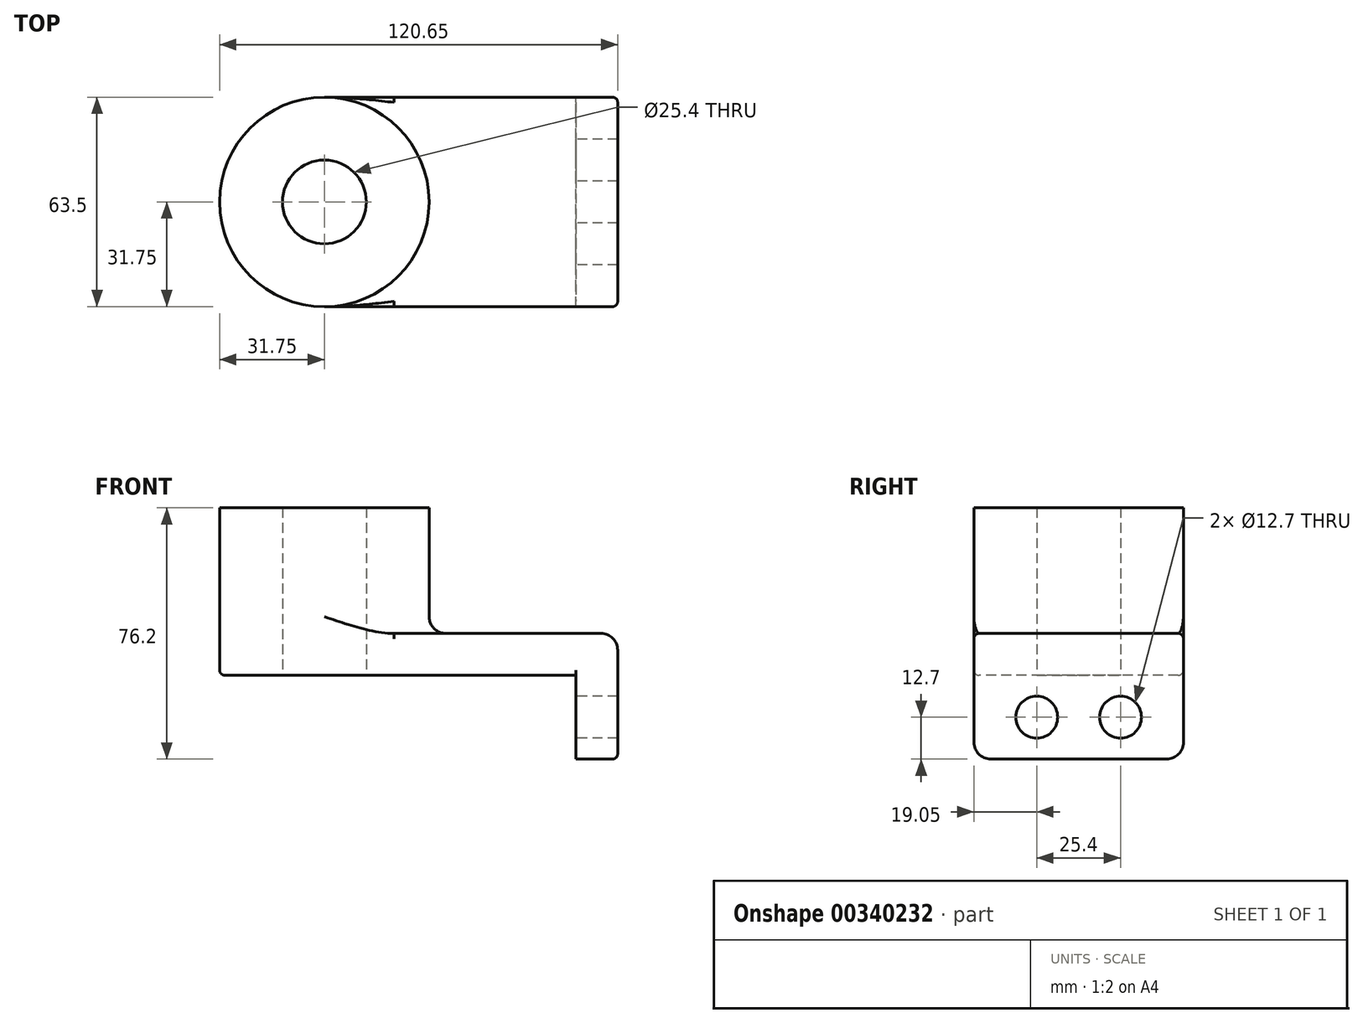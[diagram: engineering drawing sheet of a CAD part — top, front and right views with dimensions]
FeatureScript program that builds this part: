
annotation { "Feature Type Name" : "Feature", "Feature Type Description" : "" }
export const myFeature = defineFeature(function(context is Context, id is Id, definition is map)
    precondition{}
    {
        {
            var Q0;
            Q0=qCreatedBy(makeId("Top.planeOp"),FACE);
            var sketch = newSketch(context, id + "F0", { "sketchPlane" : qUnion([Q0])});
            skLineSegment(sketch, "E0.bottom", {"start": v(38.1, 31.75) * mm, "end": v(-38.1, 31.75) * mm});
            skLineSegment(sketch, "E0.top", {"start": v(38.1, -31.75) * mm, "end": v(-38.1, -31.75) * mm});
            skLineSegment(sketch, "E0.left", {"start": v(38.1, 31.75) * mm, "end": v(38.1, -31.75) * mm});
            skLineSegment(sketch, "E0.right", {"start": v(-38.1, 31.75) * mm, "end": v(-38.1, -31.75) * mm});
            skPoint(sketch, "E0.middle", {"position": v(0, 0) * mm});
            skCircle(sketch, "E1", {"center": v(-38.1, 0) * mm, "radius": 31.75 * mm});
            skCircle(sketch, "E2", {"center": v(-38.1, 0) * mm, "radius": 12.7 * mm});
            skSolve(sketch);
        }
        {
            var Q0;
            Q0 = qSketchRegion(id + "F0", true);
            extrude(context, id + "F1", {"entities" : qUnion([Q0]), "depth" : 12.7 * mm});
        }
        {
            var Q0;
            {var subQ1=sQuery(id+"F0.wireOp",EDGE,"E0.right");var subQ3=sQuery(id+"F0.wireOp",EDGE,"E2");var subQ4=makeQuery(id+"F0.imprint","INTERSECT",VERTEX,{"disambiguationData":[OD(0.0)],"derivedFrom":[subQ1,subQ3]});Q0=makeQuery(id+"F0.imprint","IMPRINT",FACE,{"disambiguationData":[TD([[makeQuery(id+"F0.imprint","IMPRINT",EDGE,{"disambiguationData":[TD([[subQ4,-1.0]])],"derivedFrom":subQ3}),-1.0]])]});}
            var Q1;
            {var subQ1=sQuery(id+"F0.wireOp",EDGE,"E0.right");var subQ3=sQuery(id+"F0.wireOp",EDGE,"E2");var subQ4=makeQuery(id+"F0.imprint","INTERSECT",VERTEX,{"disambiguationData":[OD(0.0)],"derivedFrom":[subQ1,subQ3]});Q1=makeQuery(id+"F0.imprint","IMPRINT",FACE,{"disambiguationData":[TD([[makeQuery(id+"F0.imprint","IMPRINT",EDGE,{"disambiguationData":[TD([[subQ4,1.0]])],"derivedFrom":subQ3}),-1.0]])]});}
            extrude(context, id + "F2", {"entities" : qUnion([Q0, Q1]), "operationType" : NewBodyOperationType.ADD, "depth" : 50.8 * mm});
        }
        {
            var Q0;
            Q0=makeQuery(id+"F1.opExtrude","SWEPT_FACE",FACE,{"disambiguationData":[OSD([sQuery(id+"F0.wireOp",EDGE,"E0.left")])]});
            var sketch = newSketch(context, id + "F3", { "sketchPlane" : qUnion([Q0])});
            skLineSegment(sketch, "E3.bottom", {"start": v(-31.75, 12.7) * mm, "end": v(31.75, 12.7) * mm});
            skLineSegment(sketch, "E3.top", {"start": v(-31.75, -25.4) * mm, "end": v(31.75, -25.4) * mm});
            skLineSegment(sketch, "E3.left", {"start": v(-31.75, 12.7) * mm, "end": v(-31.75, -25.4) * mm});
            skLineSegment(sketch, "E3.right", {"start": v(31.75, 12.7) * mm, "end": v(31.75, -25.4) * mm});
            skLineSegment(sketch, "E4", {"start": v(0, 0) * mm, "end": v(0, -25.4) * mm});
            skCircle(sketch, "E5", {"center": v(-12.7, -12.7) * mm, "radius": 6.35 * mm});
            skCircle(sketch, "E6.MirrorC", {"center": v(12.7, -12.7) * mm, "radius": 6.35 * mm});
            skSolve(sketch);
        }
        {
            var Q0;
            Q0 = qSketchRegion(id + "F3", true);
            extrude(context, id + "F4", {"entities" : qUnion([Q0]), "operationType" : NewBodyOperationType.ADD, "depth" : 12.7 * mm});
        }
        {
            var Q0;
            {var subQ0=sQuery(id+"F0.wireOp",EDGE,"E1");Q0=makeQuery(id+"F2.boolean.opBoolean","INTERSECT",EDGE,{"derivedFrom":[makeQuery(id+"F1.opExtrude","CAP_FACE",FACE,{"disambiguationData":[OSD([sQuery(id+"F0.wireOp",EDGE,"E0.bottom"),sQuery(id+"F0.wireOp",EDGE,"E0.top"),sQuery(id+"F0.wireOp",EDGE,"E0.left"),subQ0,sQuery(id+"F0.wireOp",EDGE,"E2")])],"isStart":false}),makeQuery(id+"F2.opExtrude","SWEPT_FACE",FACE,{"disambiguationData":[OSD([subQ0])]})]});}
            var Q1;
            Q1=makeQuery(id+"F4.opExtrude","CAP_EDGE",EDGE,{"disambiguationData":[OSD([sQuery(id+"F3.wireOp",EDGE,"E3.bottom")])],"isStart":false});
            var Q2;
            Q2=makeQuery(id+"F4.opExtrude","SWEPT_EDGE",EDGE,{"disambiguationData":[OSD([sQuery(id+"F3.wireOp",EDGE,"E3.top"),sQuery(id+"F3.wireOp",EDGE,"E3.left")])]});
            var Q3;
            Q3=makeQuery(id+"F4.opExtrude","SWEPT_EDGE",EDGE,{"disambiguationData":[OSD([sQuery(id+"F3.wireOp",EDGE,"E3.top"),sQuery(id+"F3.wireOp",EDGE,"E3.right")])]});
            fillet(context, id + "F5", {"entities" : qUnion([Q0, Q1, Q2, Q3]), "radius" : 5.08 * mm, "tangentPropagation" : true, "allowEdgeOverflow" : false});
        }
        {
            var Q0;
            Q0=makeQuery(id+"F4.boolean.opBoolean","MERGE",EDGE,{"derivedFrom":[makeQuery(id+"F1.opExtrude","CAP_EDGE",EDGE,{"disambiguationData":[OSD([sQuery(id+"F0.wireOp",EDGE,"E0.bottom")])],"isStart":false}),makeQuery(id+"F4.opExtrude","SWEPT_EDGE",EDGE,{"disambiguationData":[OSD([sQuery(id+"F3.wireOp",EDGE,"E3.bottom"),sQuery(id+"F3.wireOp",EDGE,"E3.right")])]})]});
            var Q1;
            Q1=makeQuery(id+"F4.boolean.opBoolean","MERGE",EDGE,{"derivedFrom":[makeQuery(id+"F1.opExtrude","CAP_EDGE",EDGE,{"disambiguationData":[OSD([sQuery(id+"F0.wireOp",EDGE,"E0.top")])],"isStart":false}),makeQuery(id+"F4.opExtrude","SWEPT_EDGE",EDGE,{"disambiguationData":[OSD([sQuery(id+"F3.wireOp",EDGE,"E3.bottom"),sQuery(id+"F3.wireOp",EDGE,"E3.left")])]})]});
            var Q2;
            Q2=makeQuery(id+"F1.opExtrude","CAP_EDGE",EDGE,{"disambiguationData":[OSD([sQuery(id+"F0.wireOp",EDGE,"E0.bottom")])],"isStart":true});
            var Q3;
            Q3=makeQuery(id+"F1.opExtrude","CAP_EDGE",EDGE,{"disambiguationData":[OSD([sQuery(id+"F0.wireOp",EDGE,"E0.top")])],"isStart":true});
            fillet(context, id + "F6", {"entities" : qUnion([Q0, Q1, Q2, Q3]), "radius" : 1.59 * mm, "tangentPropagation" : true, "allowEdgeOverflow" : false});
        }
    });
